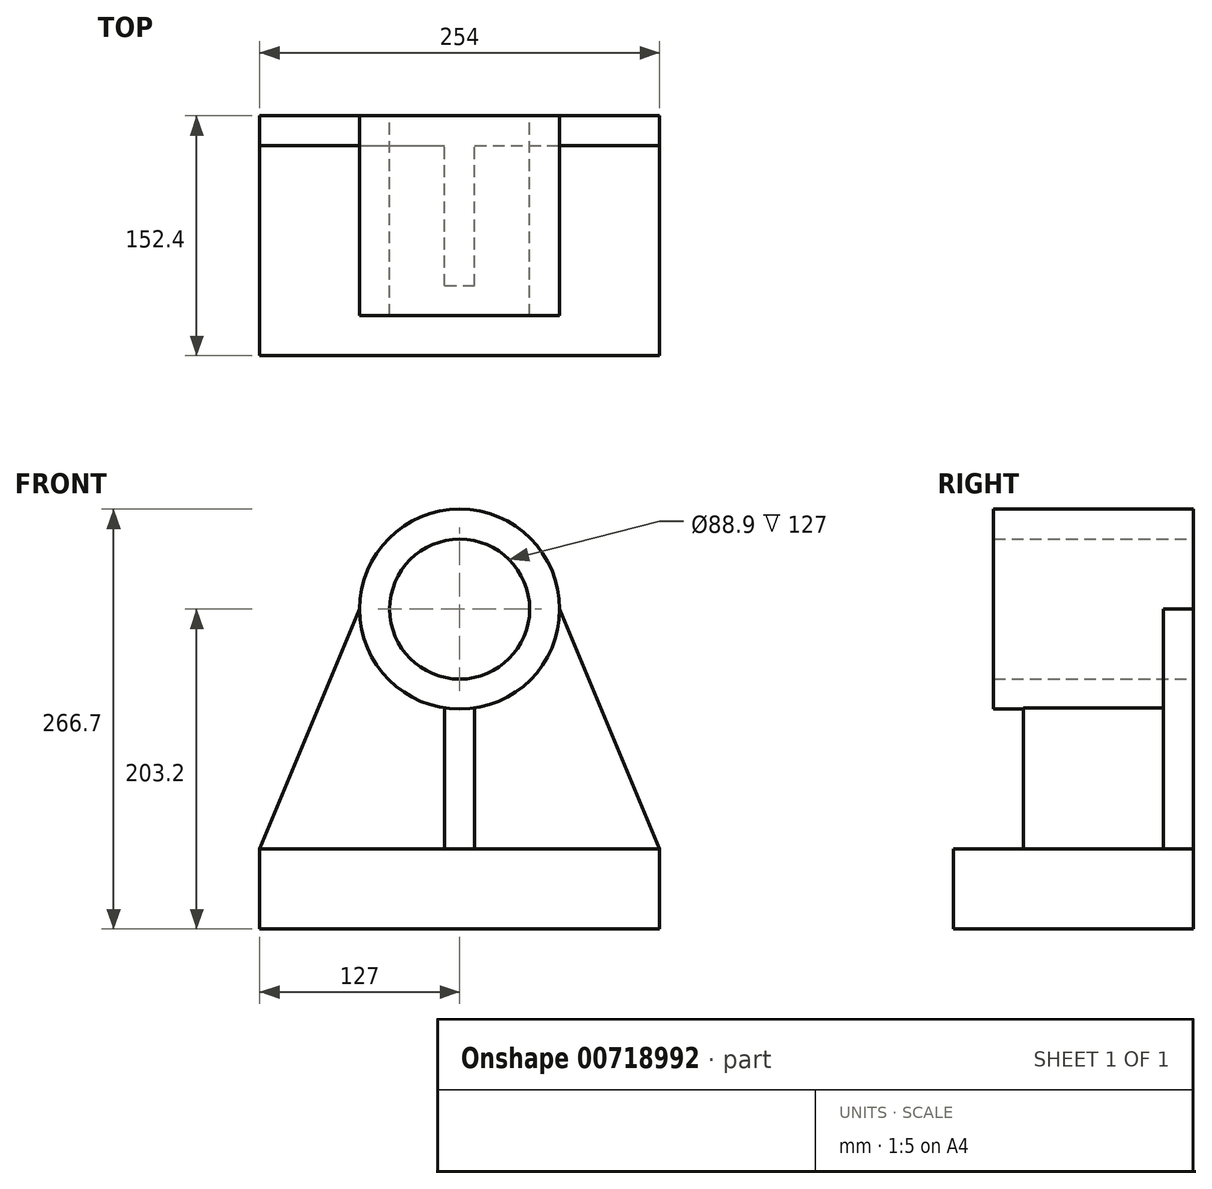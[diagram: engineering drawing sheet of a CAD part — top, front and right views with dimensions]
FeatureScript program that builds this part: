
annotation { "Feature Type Name" : "Feature", "Feature Type Description" : "" }
export const myFeature = defineFeature(function(context is Context, id is Id, definition is map)
    precondition{}
    {
        {
            var Q0;
            Q0=qCreatedBy(makeId("Front.planeOp"),FACE);
            var sketch = newSketch(context, id + "F0", { "sketchPlane" : qUnion([Q0])});
            skCircle(sketch, "E0", {"center": v(0, 0) * mm, "radius": 44.45 * mm});
            skCircle(sketch, "E1", {"center": v(0, 0) * mm, "radius": 63.5 * mm});
            skLineSegment(sketch, "E2", {"start": v(-63.5, 0) * mm, "end": v(-127, -152.4) * mm});
            skLineSegment(sketch, "E3", {"start": v(-127, -152.4) * mm, "end": v(-127, -203.2) * mm});
            skLineSegment(sketch, "E4", {"start": v(-127, -203.2) * mm, "end": v(127, -203.2) * mm});
            skLineSegment(sketch, "E5", {"start": v(127, -203.2) * mm, "end": v(127, -152.4) * mm});
            skLineSegment(sketch, "E6", {"start": v(127, -152.4) * mm, "end": v(63.5, 0) * mm});
            skLineSegment(sketch, "E7", {"start": v(-127, -152.4) * mm, "end": v(127, -152.4) * mm});
            skLineSegment(sketch, "E8", {"start": v(-9.52, -152.4) * mm, "end": v(-9.52, -62.78) * mm});
            skLineSegment(sketch, "E9", {"start": v(9.53, -152.4) * mm, "end": v(9.53, -62.78) * mm});
            skSolve(sketch);
        }
        {
            var Q0;
            {var subQ1=sQuery(id+"F0.wireOp",EDGE,"E3");Q0=makeQuery(id+"F0.imprint","IMPRINT",FACE,{"disambiguationData":[TD([[makeQuery(id+"F0.imprint","IMPRINT",EDGE,{"derivedFrom":subQ1}),1.0]])]});}
            extrude(context, id + "F1", {"entities" : qUnion([Q0]), "depth" : 152.4 * mm, "offsetDistance" : 25.4 * mm});
        }
        {
            var Q0;
            {var subQ0=sQuery(id+"F0.wireOp",EDGE,"E8");Q0=makeQuery(id+"F0.imprint","IMPRINT",FACE,{"disambiguationData":[TD([[makeQuery(id+"F0.imprint","IMPRINT",EDGE,{"derivedFrom":subQ0}),-1.0]])]});}
            extrude(context, id + "F2", {"entities" : qUnion([Q0]), "operationType" : NewBodyOperationType.ADD, "depth" : 107.95 * mm, "offsetDistance" : 25.4 * mm});
        }
        {
            var Q0;
            Q0=makeQuery(id+"F0.imprint","IMPRINT",FACE,{"disambiguationData":[TD([[makeQuery(id+"F0.imprint","IMPRINT",EDGE,{"derivedFrom":sQuery(id+"F0.wireOp",EDGE,"E0")}),-1.0]])]});
            extrude(context, id + "F3", {"entities" : qUnion([Q0]), "operationType" : NewBodyOperationType.ADD, "depth" : 127 * mm, "offsetDistance" : 25.4 * mm});
        }
        {
            var Q0;
            {var subQ0=sQuery(id+"F0.wireOp",EDGE,"E2");Q0=makeQuery(id+"F0.imprint","IMPRINT",FACE,{"disambiguationData":[TD([[makeQuery(id+"F0.imprint","IMPRINT",EDGE,{"derivedFrom":subQ0}),1.0]])]});}
            var Q1;
            {var subQ0=sQuery(id+"F0.wireOp",EDGE,"E6");Q1=makeQuery(id+"F0.imprint","IMPRINT",FACE,{"disambiguationData":[TD([[makeQuery(id+"F0.imprint","IMPRINT",EDGE,{"derivedFrom":subQ0}),1.0]])]});}
            extrude(context, id + "F4", {"entities" : qUnion([Q0, Q1]), "operationType" : NewBodyOperationType.ADD, "depth" : 19.05 * mm, "offsetDistance" : 25.4 * mm});
        }
    });
